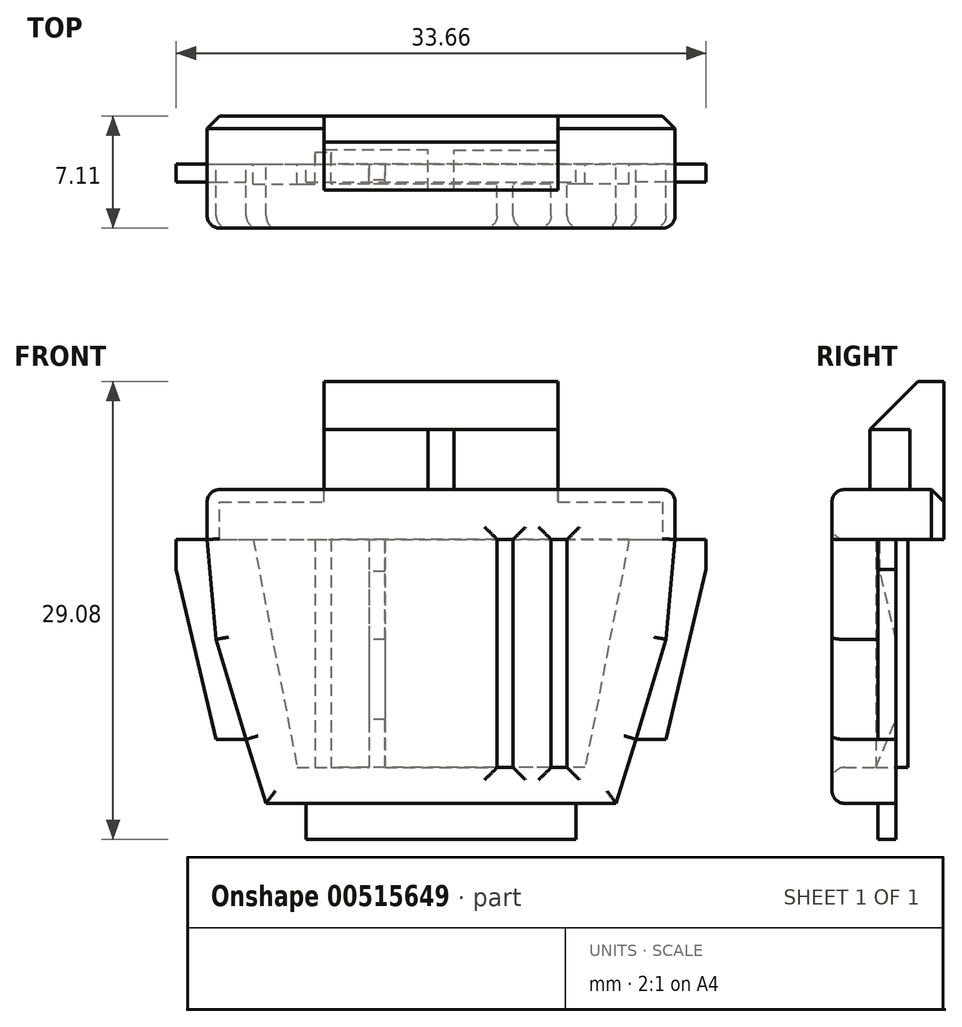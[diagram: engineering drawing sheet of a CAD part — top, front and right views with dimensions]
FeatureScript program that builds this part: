
annotation { "Feature Type Name" : "Feature", "Feature Type Description" : "" }
export const myFeature = defineFeature(function(context is Context, id is Id, definition is map)
    precondition{}
    {
        {
            var Q0;
            Q0=qCreatedBy(makeId("Front.planeOp"),FACE);
            var sketch = newSketch(context, id + "F0", { "sketchPlane" : qUnion([Q0])});
            skLineSegment(sketch, "E0", {"start": v(-14.86, 9.53) * mm, "end": v(-14.86, 6.35) * mm});
            skLineSegment(sketch, "E1", {"start": v(-14.86, 6.35) * mm, "end": v(-16.83, 6.35) * mm});
            skLineSegment(sketch, "E2", {"start": v(-16.83, 6.35) * mm, "end": v(-16.83, 4.44) * mm});
            skLineSegment(sketch, "E3", {"start": v(-16.83, 4.44) * mm, "end": v(-14.29, -6.35) * mm});
            skLineSegment(sketch, "E4", {"start": v(-14.86, 9.53) * mm, "end": v(0, 9.53) * mm});
            skLineSegment(sketch, "E5", {"start": v(-14.29, -6.35) * mm, "end": v(-12.38, -6.35) * mm});
            skLineSegment(sketch, "E6", {"start": v(-12.38, -6.35) * mm, "end": v(-11.11, -10.41) * mm});
            skLineSegment(sketch, "E7", {"start": v(-11.11, -10.41) * mm, "end": v(-8.57, -10.41) * mm});
            skLineSegment(sketch, "E8", {"start": v(-8.57, -10.41) * mm, "end": v(-8.57, -12.7) * mm});
            skLineSegment(sketch, "E9", {"start": v(-8.57, -12.7) * mm, "end": v(0, -12.7) * mm});
            skLineSegment(sketch, "E10", {"start": v(0, 9.53) * mm, "end": v(0, -12.7) * mm, "construction": true});
            skLineSegment(sketch, "E11", {"start": v(-8.57, -10.41) * mm, "end": v(0, -10.41) * mm});
            skLineSegment(sketch, "E12", {"start": v(-14.86, 6.35) * mm, "end": v(-14.29, 0) * mm});
            skLineSegment(sketch, "E13", {"start": v(-14.29, 0) * mm, "end": v(-12.38, -6.35) * mm});
            skLineSegment(sketch, "E14.MirrorCS", {"start": v(14.86, 9.53) * mm, "end": v(0, 9.53) * mm});
            skLineSegment(sketch, "E15.MirrorCS", {"start": v(14.86, 9.53) * mm, "end": v(14.86, 6.35) * mm});
            skLineSegment(sketch, "E16.MirrorCS", {"start": v(14.86, 6.35) * mm, "end": v(16.83, 6.35) * mm});
            skLineSegment(sketch, "E17.MirrorCS", {"start": v(16.83, 6.35) * mm, "end": v(16.83, 4.44) * mm});
            skLineSegment(sketch, "E18.MirrorCS", {"start": v(16.83, 4.44) * mm, "end": v(14.29, -6.35) * mm});
            skLineSegment(sketch, "E19.MirrorCS", {"start": v(14.86, 6.35) * mm, "end": v(14.29, 0) * mm});
            skLineSegment(sketch, "E20.MirrorCS", {"start": v(14.29, 0) * mm, "end": v(12.38, -6.35) * mm});
            skLineSegment(sketch, "E21.MirrorCS", {"start": v(14.29, -6.35) * mm, "end": v(12.38, -6.35) * mm});
            skLineSegment(sketch, "E22.MirrorCS", {"start": v(12.38, -6.35) * mm, "end": v(11.11, -10.41) * mm});
            skLineSegment(sketch, "E23.MirrorCS", {"start": v(11.11, -10.41) * mm, "end": v(8.57, -10.41) * mm});
            skLineSegment(sketch, "E24.MirrorCS", {"start": v(8.57, -10.41) * mm, "end": v(8.57, -12.7) * mm});
            skLineSegment(sketch, "E25.MirrorCS", {"start": v(8.57, -12.7) * mm, "end": v(0, -12.7) * mm});
            skLineSegment(sketch, "E26.MirrorCS", {"start": v(8.57, -10.41) * mm, "end": v(0, -10.41) * mm});
            skLineSegment(sketch, "E27", {"start": v(-7.43, 9.53) * mm, "end": v(-7.43, 16.38) * mm});
            skLineSegment(sketch, "E28", {"start": v(-7.43, 16.38) * mm, "end": v(0, 16.38) * mm});
            skLineSegment(sketch, "E29.MirrorCS", {"start": v(7.43, 16.38) * mm, "end": v(0, 16.38) * mm});
            skLineSegment(sketch, "E30.MirrorCS", {"start": v(7.43, 9.53) * mm, "end": v(7.43, 16.38) * mm});
            skLineSegment(sketch, "E31", {"start": v(14.86, 6.35) * mm, "end": v(0, 6.35) * mm});
            skLineSegment(sketch, "E32.MirrorCS", {"start": v(-14.86, 6.35) * mm, "end": v(0, 6.35) * mm});
            skLineSegment(sketch, "E33", {"start": v(-11.94, 6.35) * mm, "end": v(-9.14, -8.13) * mm});
            skLineSegment(sketch, "E34", {"start": v(-9.14, -8.13) * mm, "end": v(0, -8.13) * mm});
            skLineSegment(sketch, "E35.MirrorCS", {"start": v(11.94, 6.35) * mm, "end": v(9.14, -8.13) * mm});
            skLineSegment(sketch, "E36.MirrorCS", {"start": v(9.14, -8.13) * mm, "end": v(0, -8.13) * mm});
            skLineSegment(sketch, "E37.bottom", {"start": v(6.99, 6.35) * mm, "end": v(8, 6.35) * mm});
            skLineSegment(sketch, "E37.top", {"start": v(6.99, -8.13) * mm, "end": v(8, -8.13) * mm});
            skLineSegment(sketch, "E37.left", {"start": v(6.99, 6.35) * mm, "end": v(6.99, -8.13) * mm});
            skLineSegment(sketch, "E37.right", {"start": v(8, 6.35) * mm, "end": v(8, -8.13) * mm});
            skLineSegment(sketch, "E38.bottom", {"start": v(3.56, 6.35) * mm, "end": v(4.57, 6.35) * mm});
            skLineSegment(sketch, "E38.top", {"start": v(3.56, -8.13) * mm, "end": v(4.57, -8.13) * mm});
            skLineSegment(sketch, "E38.left", {"start": v(3.56, 6.35) * mm, "end": v(3.56, -8.13) * mm});
            skLineSegment(sketch, "E38.right", {"start": v(4.57, 6.35) * mm, "end": v(4.57, -8.13) * mm});
            skLineSegment(sketch, "E39.MirrorCS", {"start": v(-3.56, 6.35) * mm, "end": v(-3.56, -8.13) * mm});
            skLineSegment(sketch, "E40.MirrorCS", {"start": v(-4.57, 6.35) * mm, "end": v(-4.57, -8.13) * mm});
            skLineSegment(sketch, "E41.MirrorCS", {"start": v(-6.99, 6.35) * mm, "end": v(-6.99, -8.13) * mm});
            skLineSegment(sketch, "E42.MirrorCS", {"start": v(-8, 6.35) * mm, "end": v(-8, -8.13) * mm});
            skSolve(sketch);
        }
        {
            var Q0;
            Q0=makeQuery(id+"F0.imprint","IMPRINT",FACE,{"disambiguationData":[TD([[makeQuery(id+"F0.imprint","IMPRINT",EDGE,{"derivedFrom":sQuery(id+"F0.wireOp",EDGE,"E0")}),1.0]])]});
            var Q1;
            Q1=makeQuery(id+"F0.imprint","IMPRINT",FACE,{"disambiguationData":[TD([[makeQuery(id+"F0.imprint","IMPRINT",EDGE,{"derivedFrom":sQuery(id+"F0.wireOp",EDGE,"E6")}),1.0]])]});
            var Q2;
            {var subQ0=sQuery(id+"F0.wireOp",EDGE,"E33");Q2=makeQuery(id+"F0.imprint","IMPRINT",FACE,{"disambiguationData":[TD([[makeQuery(id+"F0.imprint","IMPRINT",EDGE,{"derivedFrom":subQ0}),1.0]])]});}
            var Q3;
            {var subQ0=sQuery(id+"F0.wireOp",EDGE,"E35.MirrorCS");Q3=makeQuery(id+"F0.imprint","IMPRINT",FACE,{"disambiguationData":[TD([[makeQuery(id+"F0.imprint","IMPRINT",EDGE,{"derivedFrom":subQ0}),-1.0]])]});}
            var Q4;
            Q4=makeQuery(id+"F0.imprint","IMPRINT",FACE,{"disambiguationData":[TD([[makeQuery(id+"F0.imprint","IMPRINT",EDGE,{"derivedFrom":sQuery(id+"F0.wireOp",EDGE,"E37.bottom")}),-1.0]])]});
            var Q5;
            {var subQ0=sQuery(id+"F0.wireOp",EDGE,"E37.left");Q5=makeQuery(id+"F0.imprint","IMPRINT",FACE,{"disambiguationData":[TD([[makeQuery(id+"F0.imprint","IMPRINT",EDGE,{"derivedFrom":subQ0}),-1.0]])]});}
            var Q6;
            Q6=makeQuery(id+"F0.imprint","IMPRINT",FACE,{"disambiguationData":[TD([[makeQuery(id+"F0.imprint","IMPRINT",EDGE,{"derivedFrom":sQuery(id+"F0.wireOp",EDGE,"E38.bottom")}),-1.0]])]});
            var Q7;
            {var subQ4=sQuery(id+"F0.wireOp",EDGE,"E38.left");Q7=makeQuery(id+"F0.imprint","IMPRINT",FACE,{"disambiguationData":[TD([[makeQuery(id+"F0.imprint","IMPRINT",EDGE,{"derivedFrom":subQ4}),-1.0]])]});}
            var Q8;
            {var subQ0=sQuery(id+"F0.wireOp",EDGE,"E39.MirrorCS");Q8=makeQuery(id+"F0.imprint","IMPRINT",FACE,{"disambiguationData":[TD([[makeQuery(id+"F0.imprint","IMPRINT",EDGE,{"derivedFrom":subQ0}),-1.0]])]});}
            var Q9;
            {var subQ0=sQuery(id+"F0.wireOp",EDGE,"E40.MirrorCS");Q9=makeQuery(id+"F0.imprint","IMPRINT",FACE,{"disambiguationData":[TD([[makeQuery(id+"F0.imprint","IMPRINT",EDGE,{"derivedFrom":subQ0}),-1.0]])]});}
            var Q10;
            {var subQ0=sQuery(id+"F0.wireOp",EDGE,"E41.MirrorCS");Q10=makeQuery(id+"F0.imprint","IMPRINT",FACE,{"disambiguationData":[TD([[makeQuery(id+"F0.imprint","IMPRINT",EDGE,{"derivedFrom":subQ0}),-1.0]])]});}
            extrude(context, id + "F1", {"entities" : qUnion([Q0, Q1, Q2, Q3, Q4, Q5, Q6, Q7, Q8, Q9, Q10]), "depth" : 4.06 * mm, "offsetDistance" : 25.4 * mm});
        }
        {
            var Q0;
            Q0=makeQuery(id+"F0.imprint","IMPRINT",FACE,{"disambiguationData":[TD([[makeQuery(id+"F0.imprint","IMPRINT",EDGE,{"derivedFrom":sQuery(id+"F0.wireOp",EDGE,"E1")}),1.0]])]});
            var Q1;
            Q1=makeQuery(id+"F0.imprint","IMPRINT",FACE,{"disambiguationData":[TD([[makeQuery(id+"F0.imprint","IMPRINT",EDGE,{"derivedFrom":sQuery(id+"F0.wireOp",EDGE,"E8")}),1.0]])]});
            var Q2;
            Q2=makeQuery(id+"F0.imprint","IMPRINT",FACE,{"disambiguationData":[TD([[makeQuery(id+"F0.imprint","IMPRINT",EDGE,{"derivedFrom":sQuery(id+"F0.wireOp",EDGE,"E16.MirrorCS")}),-1.0]])]});
            extrude(context, id + "F2", {"entities" : qUnion([Q0, Q1, Q2]), "operationType" : NewBodyOperationType.ADD, "depth" : 1.14 * mm, "offsetDistance" : 25.4 * mm});
        }
        {
            var Q0;
            {var subQ0=sQuery(id+"F0.wireOp",EDGE,"E27");Q0=makeQuery(id+"F0.imprint","IMPRINT",FACE,{"disambiguationData":[TD([[makeQuery(id+"F0.imprint","IMPRINT",EDGE,{"derivedFrom":subQ0}),-1.0]])]});}
            extrude(context, id + "F3", {"entities" : qUnion([Q0]), "operationType" : NewBodyOperationType.ADD, "depth" : 1.65 * mm, "offsetDistance" : 25.4 * mm});
        }
        {
            var Q0;
            {var subQ0=sQuery(id+"F0.wireOp",EDGE,"E27");Q0=makeQuery(id+"F0.imprint","IMPRINT",FACE,{"disambiguationData":[TD([[makeQuery(id+"F0.imprint","IMPRINT",EDGE,{"derivedFrom":subQ0}),-1.0]])]});}
            extrude(context, id + "F4", {"entities" : qUnion([Q0]), "operationType" : NewBodyOperationType.ADD, "oppositeDirection" : true, "depth" : 3.05 * mm, "offsetDistance" : 25.4 * mm});
        }
        {
            var Q0;
            {var subQ4=sQuery(id+"F0.wireOp",EDGE,"E0");Q0=makeQuery(id+"F0.imprint","IMPRINT",FACE,{"disambiguationData":[TD([[makeQuery(id+"F0.imprint","IMPRINT",EDGE,{"derivedFrom":subQ4}),1.0]])]});}
            extrude(context, id + "F5", {"entities" : qUnion([Q0]), "operationType" : NewBodyOperationType.ADD, "oppositeDirection" : true, "depth" : 3.05 * mm, "offsetDistance" : 25.4 * mm});
        }
        {
            var Q0;
            Q0=makeQuery(id+"F3.opExtrude","CAP_EDGE",EDGE,{"disambiguationData":[OSD([sQuery(id+"F0.wireOp",EDGE,"E28"),sQuery(id+"F0.wireOp",EDGE,"E29.MirrorCS")])],"isStart":false});
            chamfer(context, id + "F6", {"entities" : qUnion([Q0]), "width" : 3.05 * mm, "tangentPropagation" : true});
        }
        {
            var Q0;
            Q0=makeQuery(id+"F3.opExtrude","CAP_FACE",FACE,{"disambiguationData":[OSD([sQuery(id+"F0.wireOp",EDGE,"E4"),sQuery(id+"F0.wireOp",EDGE,"E14.MirrorCS"),sQuery(id+"F0.wireOp",EDGE,"E27"),sQuery(id+"F0.wireOp",EDGE,"E28"),sQuery(id+"F0.wireOp",EDGE,"E29.MirrorCS"),sQuery(id+"F0.wireOp",EDGE,"E30.MirrorCS")])],"isStart":false});
            extrude(context, id + "F7", {"entities" : qUnion([Q0]), "operationType" : NewBodyOperationType.REMOVE, "oppositeDirection" : true, "depth" : 2.54 * mm, "offsetDistance" : 25.4 * mm});
        }
        {
            var Q0;
            Q0=makeQuery(id+"F7.boolean.opBoolean","COPY",FACE,{"derivedFrom":makeQuery(id+"F7.opExtrude","CAP_FACE",FACE,{"disambiguationData":[OSD([sQuery(id+"F0.wireOp",EDGE,"E4"),sQuery(id+"F0.wireOp",EDGE,"E14.MirrorCS"),sQuery(id+"F0.wireOp",EDGE,"E27"),sQuery(id+"F0.wireOp",EDGE,"E28"),sQuery(id+"F0.wireOp",EDGE,"E29.MirrorCS"),sQuery(id+"F0.wireOp",EDGE,"E30.MirrorCS")])],"isStart":false})});
            var sketch = newSketch(context, id + "F8", { "sketchPlane" : qUnion([Q0])});
            skLineSegment(sketch, "E43", {"start": v(0, 13.34) * mm, "end": v(0, 9.53) * mm, "construction": true});
            skLineSegment(sketch, "E44", {"start": v(-7.43, 11.43) * mm, "end": v(7.43, 11.43) * mm, "construction": true});
            skLineSegment(sketch, "E45.bottom", {"start": v(-0.83, 9.53) * mm, "end": v(0.83, 9.53) * mm});
            skLineSegment(sketch, "E45.top", {"start": v(-0.83, 13.34) * mm, "end": v(0.83, 13.34) * mm});
            skLineSegment(sketch, "E45.left", {"start": v(-0.83, 9.53) * mm, "end": v(-0.83, 13.34) * mm});
            skLineSegment(sketch, "E45.right", {"start": v(0.83, 9.53) * mm, "end": v(0.83, 13.34) * mm});
            skPoint(sketch, "E45.middle", {"position": v(0, 11.43) * mm});
            skSolve(sketch);
        }
        {
            var Q0;
            Q0=makeQuery(id+"F8.imprint","IMPRINT",FACE,{"disambiguationData":[TD([[makeQuery(id+"F8.imprint","IMPRINT",EDGE,{"derivedFrom":sQuery(id+"F8.wireOp",EDGE,"E45.bottom")}),1.0]])]});
            var Q1;
            {var subQ0=sQuery(id+"F0.wireOp",EDGE,"E27");var subQ1=sQuery(id+"F0.wireOp",EDGE,"E30.MirrorCS");var subQ2=sQuery(id+"F0.wireOp",EDGE,"E29.MirrorCS");var subQ3=sQuery(id+"F0.wireOp",EDGE,"E28");var subQ4=sQuery(id+"F0.wireOp",EDGE,"E14.MirrorCS");var subQ5=sQuery(id+"F0.wireOp",EDGE,"E4");var subQ6=makeQuery(id+"F6.opChamfer","BLEND_VERTEX",VERTEX,{"blendedFrom":[makeQuery(id+"F3.opExtrude","CAP_EDGE",EDGE,{"disambiguationData":[OSD([subQ3,subQ2])],"isStart":false}),makeQuery(id+"F3.opExtrude","CAP_FACE",FACE,{"disambiguationData":[OSD([subQ5,subQ4,subQ0,subQ3,subQ2,subQ1])],"isStart":false}),makeQuery(id+"F4.boolean.opBoolean","MERGE",FACE,{"derivedFrom":[makeQuery(id+"F3.opExtrude","SWEPT_FACE",FACE,{"disambiguationData":[OSD([subQ0])]}),makeQuery(id+"F4.opExtrude","SWEPT_FACE",FACE,{"disambiguationData":[OSD([subQ0])]})]})],"blendedInto":[makeQuery(id+"F3.opExtrude","CAP_FACE",FACE,{"disambiguationData":[OSD([subQ5,subQ4,subQ0,subQ3,subQ2,subQ1])],"isStart":false}),makeQuery(id+"F4.boolean.opBoolean","MERGE",FACE,{"derivedFrom":[makeQuery(id+"F3.opExtrude","SWEPT_FACE",FACE,{"disambiguationData":[OSD([subQ0])]}),makeQuery(id+"F4.opExtrude","SWEPT_FACE",FACE,{"disambiguationData":[OSD([subQ0])]})]})]});Q1=makeQuery(id+"F7.boolean.opBoolean","MERGE",VERTEX,{"derivedFrom":[subQ6,makeQuery(id+"F7.opExtrude","CAP_VERTEX",VERTEX,{"disambiguationData":[OSD([subQ5,subQ4,subQ0,subQ3,subQ2,subQ1]),TDD([subQ6])],"isStart":true})]});}
            extrude(context, id + "F9", {"entities" : qUnion([Q0]), "operationType" : NewBodyOperationType.ADD, "endBound" : BoundingType.UP_TO_VERTEX, "depth" : 25.4 * mm, "endBoundEntityVertex" : qUnion([Q1]), "offsetDistance" : 25.4 * mm});
        }
        {
            var Q0;
            {var subQ0=sQuery(id+"F0.wireOp",EDGE,"E35.MirrorCS");Q0=makeQuery(id+"F0.imprint","IMPRINT",FACE,{"disambiguationData":[TD([[makeQuery(id+"F0.imprint","IMPRINT",EDGE,{"derivedFrom":subQ0}),-1.0]])]});}
            var Q1;
            {var subQ0=sQuery(id+"F0.wireOp",EDGE,"E37.left");Q1=makeQuery(id+"F0.imprint","IMPRINT",FACE,{"disambiguationData":[TD([[makeQuery(id+"F0.imprint","IMPRINT",EDGE,{"derivedFrom":subQ0}),-1.0]])]});}
            var Q2;
            {var subQ4=sQuery(id+"F0.wireOp",EDGE,"E38.left");Q2=makeQuery(id+"F0.imprint","IMPRINT",FACE,{"disambiguationData":[TD([[makeQuery(id+"F0.imprint","IMPRINT",EDGE,{"derivedFrom":subQ4}),-1.0]])]});}
            var Q3;
            {var subQ0=sQuery(id+"F0.wireOp",EDGE,"E40.MirrorCS");Q3=makeQuery(id+"F0.imprint","IMPRINT",FACE,{"disambiguationData":[TD([[makeQuery(id+"F0.imprint","IMPRINT",EDGE,{"derivedFrom":subQ0}),-1.0]])]});}
            var Q4;
            {var subQ0=sQuery(id+"F0.wireOp",EDGE,"E33");Q4=makeQuery(id+"F0.imprint","IMPRINT",FACE,{"disambiguationData":[TD([[makeQuery(id+"F0.imprint","IMPRINT",EDGE,{"derivedFrom":subQ0}),1.0]])]});}
            var Q5;
            Q5=makeQuery(id+"F0.imprint","IMPRINT",FACE,{"disambiguationData":[TD([[makeQuery(id+"F0.imprint","IMPRINT",EDGE,{"derivedFrom":sQuery(id+"F0.wireOp",EDGE,"E38.bottom")}),-1.0]])]});
            var Q6;
            {var subQ0=sQuery(id+"F0.wireOp",EDGE,"E39.MirrorCS");Q6=makeQuery(id+"F0.imprint","IMPRINT",FACE,{"disambiguationData":[TD([[makeQuery(id+"F0.imprint","IMPRINT",EDGE,{"derivedFrom":subQ0}),-1.0]])]});}
            extrude(context, id + "F10", {"entities" : qUnion([Q0, Q1, Q2, Q3, Q4, Q5, Q6]), "operationType" : NewBodyOperationType.REMOVE, "depth" : 1.27 * mm, "offsetDistance" : 25.4 * mm});
        }
        {
            var Q0;
            Q0=makeQuery(id+"F0.imprint","IMPRINT",FACE,{"disambiguationData":[TD([[makeQuery(id+"F0.imprint","IMPRINT",EDGE,{"derivedFrom":sQuery(id+"F0.wireOp",EDGE,"E37.bottom")}),-1.0]])]});
            var Q1;
            {var subQ0=sQuery(id+"F0.wireOp",EDGE,"E41.MirrorCS");Q1=makeQuery(id+"F0.imprint","IMPRINT",FACE,{"disambiguationData":[TD([[makeQuery(id+"F0.imprint","IMPRINT",EDGE,{"derivedFrom":subQ0}),-1.0]])]});}
            extrude(context, id + "F11", {"entities" : qUnion([Q0, Q1]), "operationType" : NewBodyOperationType.ADD, "oppositeDirection" : true, "depth" : 0.76 * mm, "offsetDistance" : 25.4 * mm});
        }
        {
            var Q0;
            Q0=makeQuery(id+"F0.imprint","IMPRINT",FACE,{"disambiguationData":[TD([[makeQuery(id+"F0.imprint","IMPRINT",EDGE,{"derivedFrom":sQuery(id+"F0.wireOp",EDGE,"E38.bottom")}),-1.0]])]});
            var Q1;
            {var subQ0=sQuery(id+"F0.wireOp",EDGE,"E39.MirrorCS");Q1=makeQuery(id+"F0.imprint","IMPRINT",FACE,{"disambiguationData":[TD([[makeQuery(id+"F0.imprint","IMPRINT",EDGE,{"derivedFrom":subQ0}),-1.0]])]});}
            extrude(context, id + "F12", {"entities" : qUnion([Q0, Q1]), "operationType" : NewBodyOperationType.ADD, "depth" : 1.27 * mm, "offsetDistance" : 25.4 * mm});
        }
        {
            var Q0;
            Q0=makeQuery(id+"F12.opExtrude","SWEPT_FACE",FACE,{"disambiguationData":[OSD([sQuery(id+"F0.wireOp",EDGE,"E40.MirrorCS")])]});
            var sketch = newSketch(context, id + "F13", { "sketchPlane" : qUnion([Q0])});
            skLineSegment(sketch, "E46", {"start": v(1.02, 6.35) * mm, "end": v(1.02, 4.32) * mm});
            skLineSegment(sketch, "E47", {"start": v(1.02, 4.32) * mm, "end": v(0, 0) * mm});
            skLineSegment(sketch, "E48", {"start": v(0, 0) * mm, "end": v(0, -5.08) * mm});
            skLineSegment(sketch, "E49", {"start": v(0, -5.08) * mm, "end": v(1.27, -8.13) * mm});
            skSolve(sketch);
        }
        {
            var Q0;
            {var subQ0=sQuery(id+"F13.wireOp",EDGE,"E46");Q0=makeQuery(id+"F13.imprint","IMPRINT",FACE,{"disambiguationData":[TD([[makeQuery(id+"F13.imprint","IMPRINT",EDGE,{"derivedFrom":subQ0}),-1.0]])]});}
            var Q1;
            {var subQ0=sQuery(id+"F13.wireOp",EDGE,"E49");Q1=makeQuery(id+"F13.imprint","IMPRINT",FACE,{"disambiguationData":[TD([[makeQuery(id+"F13.imprint","IMPRINT",EDGE,{"derivedFrom":subQ0}),-1.0]])]});}
            extrude(context, id + "F14", {"entities" : qUnion([Q0, Q1]), "operationType" : NewBodyOperationType.REMOVE, "oppositeDirection" : true, "depth" : 9.52 * mm, "offsetDistance" : 25.4 * mm});
        }
        {
            var Q0;
            Q0=makeQuery(id+"F1.opExtrude","CAP_FACE",FACE,{"disambiguationData":[OSD([sQuery(id+"F0.wireOp",EDGE,"E0"),sQuery(id+"F0.wireOp",EDGE,"E4"),sQuery(id+"F0.wireOp",EDGE,"E6"),sQuery(id+"F0.wireOp",EDGE,"E7"),sQuery(id+"F0.wireOp",EDGE,"E11"),sQuery(id+"F0.wireOp",EDGE,"E12"),sQuery(id+"F0.wireOp",EDGE,"E13"),sQuery(id+"F0.wireOp",EDGE,"E14.MirrorCS"),sQuery(id+"F0.wireOp",EDGE,"E15.MirrorCS"),sQuery(id+"F0.wireOp",EDGE,"E19.MirrorCS"),sQuery(id+"F0.wireOp",EDGE,"E20.MirrorCS"),sQuery(id+"F0.wireOp",EDGE,"E22.MirrorCS"),sQuery(id+"F0.wireOp",EDGE,"E23.MirrorCS"),sQuery(id+"F0.wireOp",EDGE,"E26.MirrorCS")])],"isStart":false});
            var Q1;
            {var subQ0=sQuery(id+"F0.wireOp",EDGE,"E4");var subQ1=sQuery(id+"F0.wireOp",EDGE,"E0");Q1=makeQuery(id+"F5.boolean.opBoolean","MERGE",EDGE,{"derivedFrom":[makeQuery(id+"F1.opExtrude","SWEPT_EDGE",EDGE,{"disambiguationData":[OSD([subQ1,subQ0])]}),makeQuery(id+"F5.opExtrude","SWEPT_EDGE",EDGE,{"disambiguationData":[OSD([subQ1,subQ0])]})]});}
            var Q2;
            {var subQ0=sQuery(id+"F0.wireOp",EDGE,"E15.MirrorCS");var subQ1=sQuery(id+"F0.wireOp",EDGE,"E14.MirrorCS");Q2=makeQuery(id+"F5.boolean.opBoolean","MERGE",EDGE,{"derivedFrom":[makeQuery(id+"F1.opExtrude","SWEPT_EDGE",EDGE,{"disambiguationData":[OSD([subQ1,subQ0])]}),makeQuery(id+"F5.opExtrude","SWEPT_EDGE",EDGE,{"disambiguationData":[OSD([subQ1,subQ0])]})]});}
            fillet(context, id + "F15", {"entities" : qUnion([Q0, Q1, Q2]), "radius" : 0.8 * mm, "tangentPropagation" : true, "allowEdgeOverflow" : false});
        }
        {
            var Q0;
            {var subQ1=sQuery(id+"F0.wireOp",EDGE,"E14.MirrorCS");var subQ2=sQuery(id+"F0.wireOp",EDGE,"E4");var subQ3=sQuery(id+"F0.wireOp",EDGE,"E15.MirrorCS");Q0=makeQuery(id+"F5.boolean.opBoolean","SPLIT",EDGE,{"disambiguationData":[TD([makeQuery(id+"F1.opExtrude","SWEPT_FACE",FACE,{"disambiguationData":[OSD([subQ3])]})])],"derivedFrom":makeQuery(id+"F5.opExtrude","CAP_EDGE",EDGE,{"disambiguationData":[OSD([subQ2,subQ1])],"isStart":false})});}
            var Q1;
            {var subQ1=sQuery(id+"F0.wireOp",EDGE,"E14.MirrorCS");var subQ2=sQuery(id+"F0.wireOp",EDGE,"E4");var subQ3=sQuery(id+"F0.wireOp",EDGE,"E0");Q1=makeQuery(id+"F5.boolean.opBoolean","SPLIT",EDGE,{"disambiguationData":[TD([makeQuery(id+"F1.opExtrude","SWEPT_FACE",FACE,{"disambiguationData":[OSD([subQ3])]})])],"derivedFrom":makeQuery(id+"F5.opExtrude","CAP_EDGE",EDGE,{"disambiguationData":[OSD([subQ2,subQ1])],"isStart":false})});}
            chamfer(context, id + "F16", {"entities" : qUnion([Q0, Q1]), "width" : 0.8 * mm, "tangentPropagation" : true});
        }
    });
